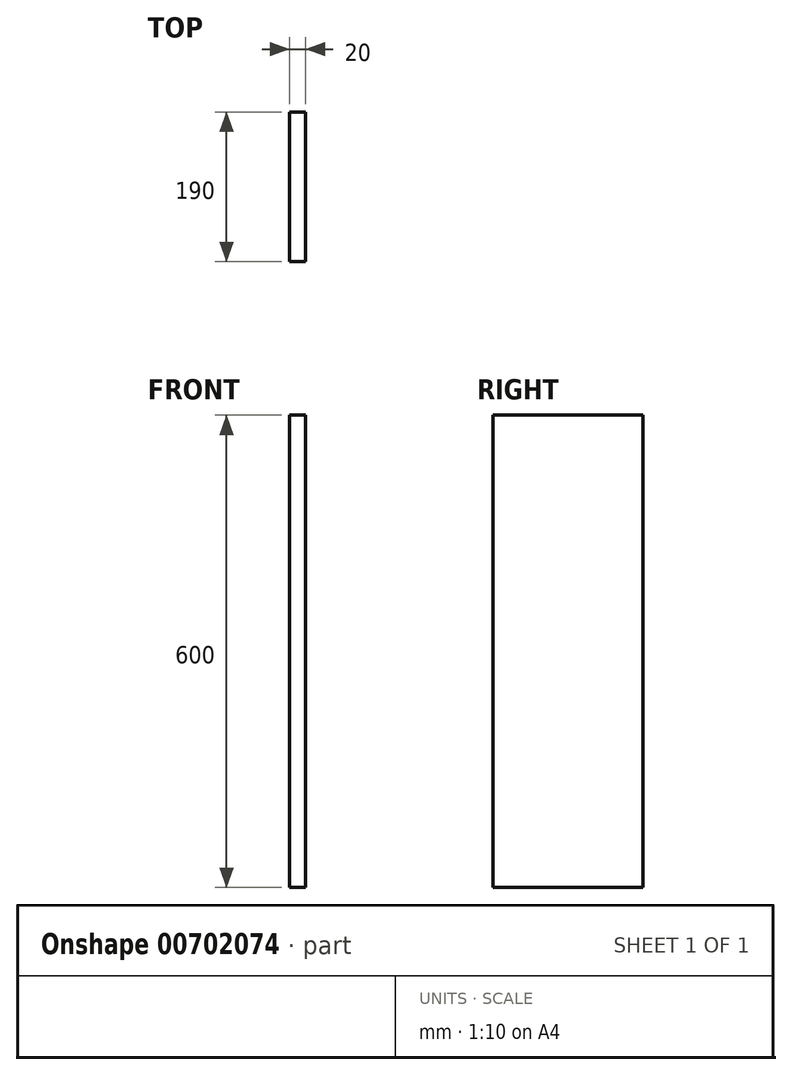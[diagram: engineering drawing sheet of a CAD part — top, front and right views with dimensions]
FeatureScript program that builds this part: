
annotation { "Feature Type Name" : "Feature", "Feature Type Description" : "" }
export const myFeature = defineFeature(function(context is Context, id is Id, definition is map)
    precondition{}
    {
        {
            var Q0;
            Q0=qCreatedBy(makeId("Right.planeOp"),FACE);
            var sketch = newSketch(context, id + "F0", { "sketchPlane" : qUnion([Q0])});
            skLineSegment(sketch, "E0.bottom", {"start": v(0, 0) * mm, "end": v(190, 0) * mm});
            skLineSegment(sketch, "E0.top", {"start": v(0, 600) * mm, "end": v(190, 600) * mm});
            skLineSegment(sketch, "E0.left", {"start": v(0, 0) * mm, "end": v(0, 600) * mm});
            skLineSegment(sketch, "E0.right", {"start": v(190, 0) * mm, "end": v(190, 600) * mm});
            skSolve(sketch);
        }
        {
            var Q0;
            Q0=qSketchRegion(id+"F0",true);
            extrude(context, id + "F1", {"entities" : qUnion([Q0]), "depth" : 20 * mm, "offsetDistance" : 25 * mm});
        }
    });
